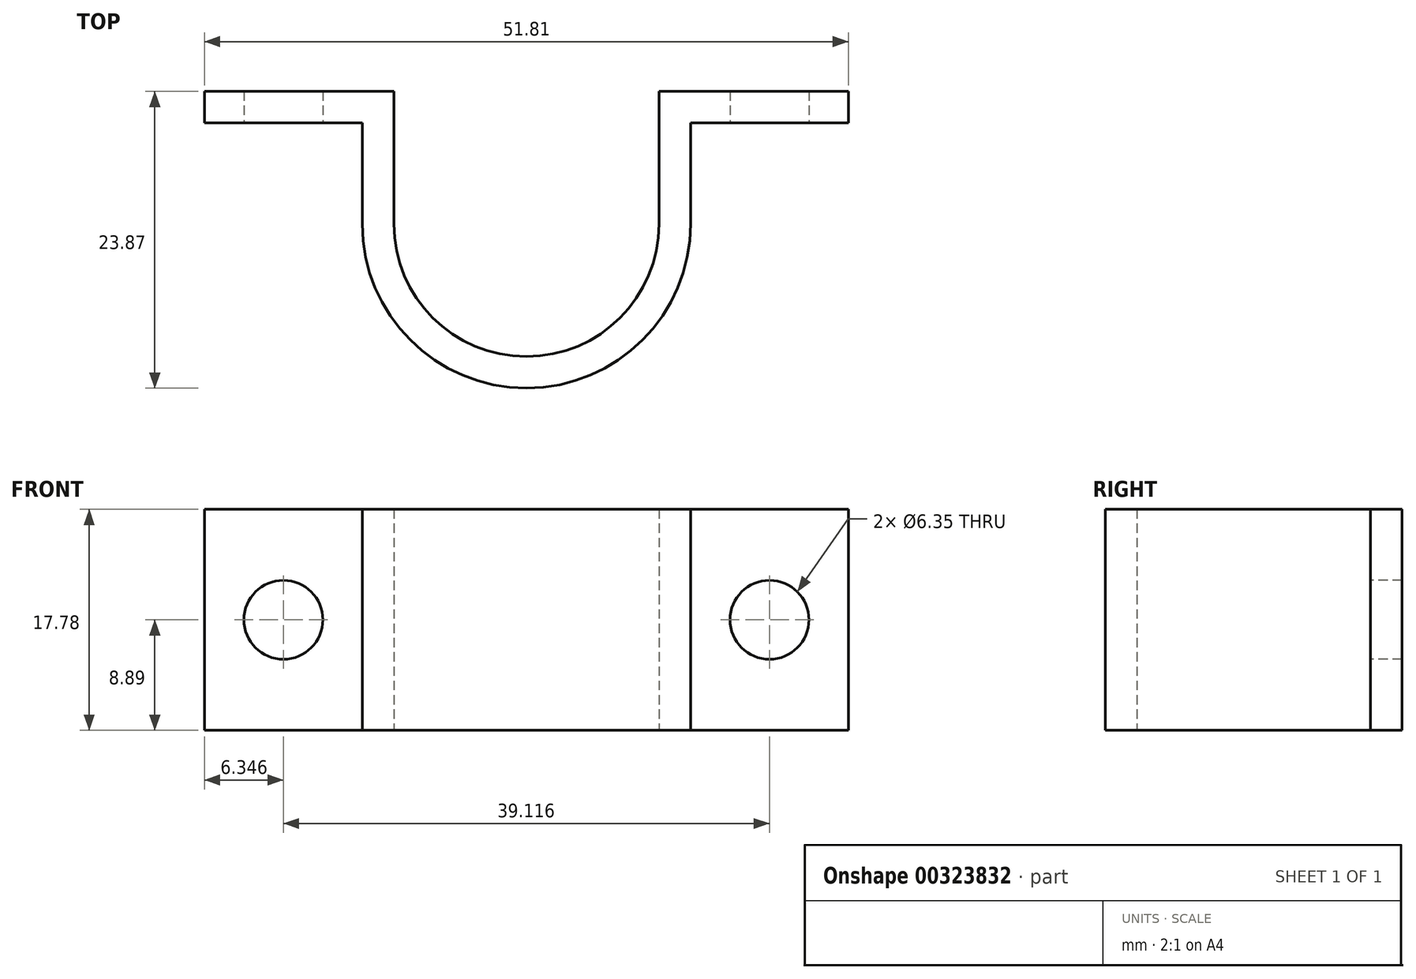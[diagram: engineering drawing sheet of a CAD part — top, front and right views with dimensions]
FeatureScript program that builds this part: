
annotation { "Feature Type Name" : "Feature", "Feature Type Description" : "" }
export const myFeature = defineFeature(function(context is Context, id is Id, definition is map)
    precondition{}
    {
        {
            var Q0;
            Q0=qCreatedBy(makeId("Top.planeOp"),FACE);
            var sketch = newSketch(context, id + "F0", { "sketchPlane" : qUnion([Q0])});
            skLineSegment(sketch, "E0.top", {"start": v(-29.5, -14.94) * mm, "end": v(-16.8, -14.94) * mm});
            skArc(sketch, "E1", {"start": v(-14.26, -25.6) * mm, "mid": v(-3.6, -36.27) * mm, "end": v(7.07, -25.6) * mm});
            skPoint(sketch, "E1.centerSnap0", {"position": v(-3.6, -14.94) * mm});
            skLineSegment(sketch, "E2", {"start": v(-14.26, -14.94) * mm, "end": v(-14.26, -25.6) * mm});
            skLineSegment(sketch, "E3", {"start": v(7.07, -14.94) * mm, "end": v(7.07, -25.6) * mm});
            skLineSegment(sketch, "E4.0", {"start": v(9.61, -17.48) * mm, "end": v(9.61, -25.6) * mm});
            skArc(sketch, "E4.1", {"start": v(-16.8, -25.6) * mm, "mid": v(-3.6, -38.81) * mm, "end": v(9.61, -25.6) * mm});
            skLineSegment(sketch, "E4.2", {"start": v(-16.8, -17.48) * mm, "end": v(-16.8, -25.6) * mm});
            skLineSegment(sketch, "E5.trimOffspring", {"start": v(9.61, -14.94) * mm, "end": v(22.31, -14.94) * mm});
            skLineSegment(sketch, "E6.bottom", {"start": v(-14.26, -14.94) * mm, "end": v(-29.5, -14.94) * mm});
            skLineSegment(sketch, "E6.top", {"start": v(-16.8, -17.48) * mm, "end": v(-29.5, -17.48) * mm});
            skLineSegment(sketch, "E6.right", {"start": v(-29.5, -14.94) * mm, "end": v(-29.5, -17.48) * mm});
            skLineSegment(sketch, "E7.bottom", {"start": v(7.07, -14.94) * mm, "end": v(22.31, -14.94) * mm});
            skLineSegment(sketch, "E7.top", {"start": v(9.61, -17.48) * mm, "end": v(22.31, -17.48) * mm});
            skLineSegment(sketch, "E7.right", {"start": v(22.31, -14.94) * mm, "end": v(22.31, -17.48) * mm});
            skSolve(sketch);
        }
        {
            var Q0;
            Q0=makeQuery(id+"F0.imprint","IMPRINT",FACE,{"disambiguationData":[TD([[makeQuery(id+"F0.imprint","IMPRINT",EDGE,{"derivedFrom":sQuery(id+"F0.wireOp",EDGE,"E1")}),-1.0]])]});
            extrude(context, id + "F1", {"entities" : qUnion([Q0]), "depth" : 17.78 * mm});
        }
        {
            var Q0;
            Q0=makeQuery(id+"F1.opExtrude","SWEPT_FACE",FACE,{"disambiguationData":[OSD([sQuery(id+"F0.wireOp",EDGE,"E6.top")])]});
            var sketch = newSketch(context, id + "F2", { "sketchPlane" : qUnion([Q0])});
            skCircle(sketch, "E8", {"center": v(-23.15, 8.9) * mm, "radius": 3.18 * mm});
            skCircle(sketch, "E9", {"center": v(15.96, 8.9) * mm, "radius": 3.18 * mm});
            skSolve(sketch);
        }
        {
            var Q0;
            Q0=makeQuery(id+"F2.imprint","IMPRINT",FACE,{"disambiguationData":[TD([[makeQuery(id+"F2.imprint","IMPRINT",EDGE,{"derivedFrom":sQuery(id+"F2.wireOp",EDGE,"E8")}),1.0]])]});
            var Q1;
            Q1=makeQuery(id+"F2.imprint","IMPRINT",FACE,{"disambiguationData":[TD([[makeQuery(id+"F2.imprint","IMPRINT",EDGE,{"derivedFrom":sQuery(id+"F2.wireOp",EDGE,"E9")}),1.0]])]});
            extrude(context, id + "F3", {"entities" : qUnion([Q0, Q1]), "operationType" : NewBodyOperationType.REMOVE, "endBound" : BoundingType.THROUGH_ALL, "oppositeDirection" : true, "depth" : 25.4 * mm});
        }
    });
